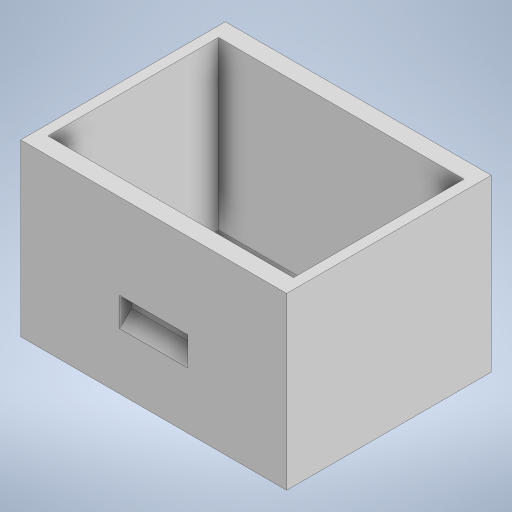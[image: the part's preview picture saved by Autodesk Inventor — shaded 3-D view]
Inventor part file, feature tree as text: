
AUTODESK INVENTOR PART (.ipt)
format: ipt  version: 2023.1 (Build 271208000, 208)  size: 214,528 bytes
history: native  units: mm
features: extrude x4, sketch x4, chamfer x2, mirror x1
ambient origin geometry x8: Origin, YZ Plane, XZ Plane, XY Plane, X Axis, Y Axis, Z Axis, Center Point
bodies: 实体1 (feature_tree)
feature tree (11):
  extrude  "拉伸1"  Depth=390.0mm
  extrude  "拉伸2"  Depth=360.0mm
  extrude  "拉伸3"  Depth=245.0mm TaperAngle=0.0deg
  extrude  "拉伸4"  Depth=5.0mm
  mirror  "镜像1"
  chamfer  "倒角1"  Distance=17.0mm
  chamfer  "倒角2"  Distance=5.0mm
  sketch  "草图1"  dims[d0=250.0mm d1=390.0mm]
  sketch  "草图2"  dims[d2=300.0mm d3=0.0mm d4=360.0mm]
  sketch  "草图3"  dims[d5=250.0mm d6=245.0mm d7=0.0mm]
  sketch  "草图4"  dims[d8=100.0mm d9=50.0mm d10=17.0mm d11=0.0mm d12=5.0mm d13=0.0mm d14=17.0mm d15=2.0mm d16=45.0deg d17=5.0mm d18=2.0mm d19=45.0deg d20=0.0mm d21=0.0mm d22=0.0mm d23=0.0mm]
